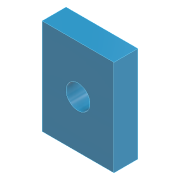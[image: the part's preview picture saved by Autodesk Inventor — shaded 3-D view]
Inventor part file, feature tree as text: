
AUTODESK INVENTOR PART (.ipt)
format: ipt  version: 2021 (Build 250183000, 183)  size: 82,944 bytes
history: native  units: mm
features: extrude x1, sketch x1
ambient origin geometry x8: Origin, YZ Plane, XZ Plane, XY Plane, X Axis, Y Axis, Z Axis, Center Point
bodies: Solid1 (feature_tree)
feature tree (2):
  extrude  "Extrusion1"  Depth=30.0mm
  sketch  "Sketch1"  dims[d0=10.0mm d1=30.0mm d2=40.0mm d3=10.0mm d4=0.0mm]
